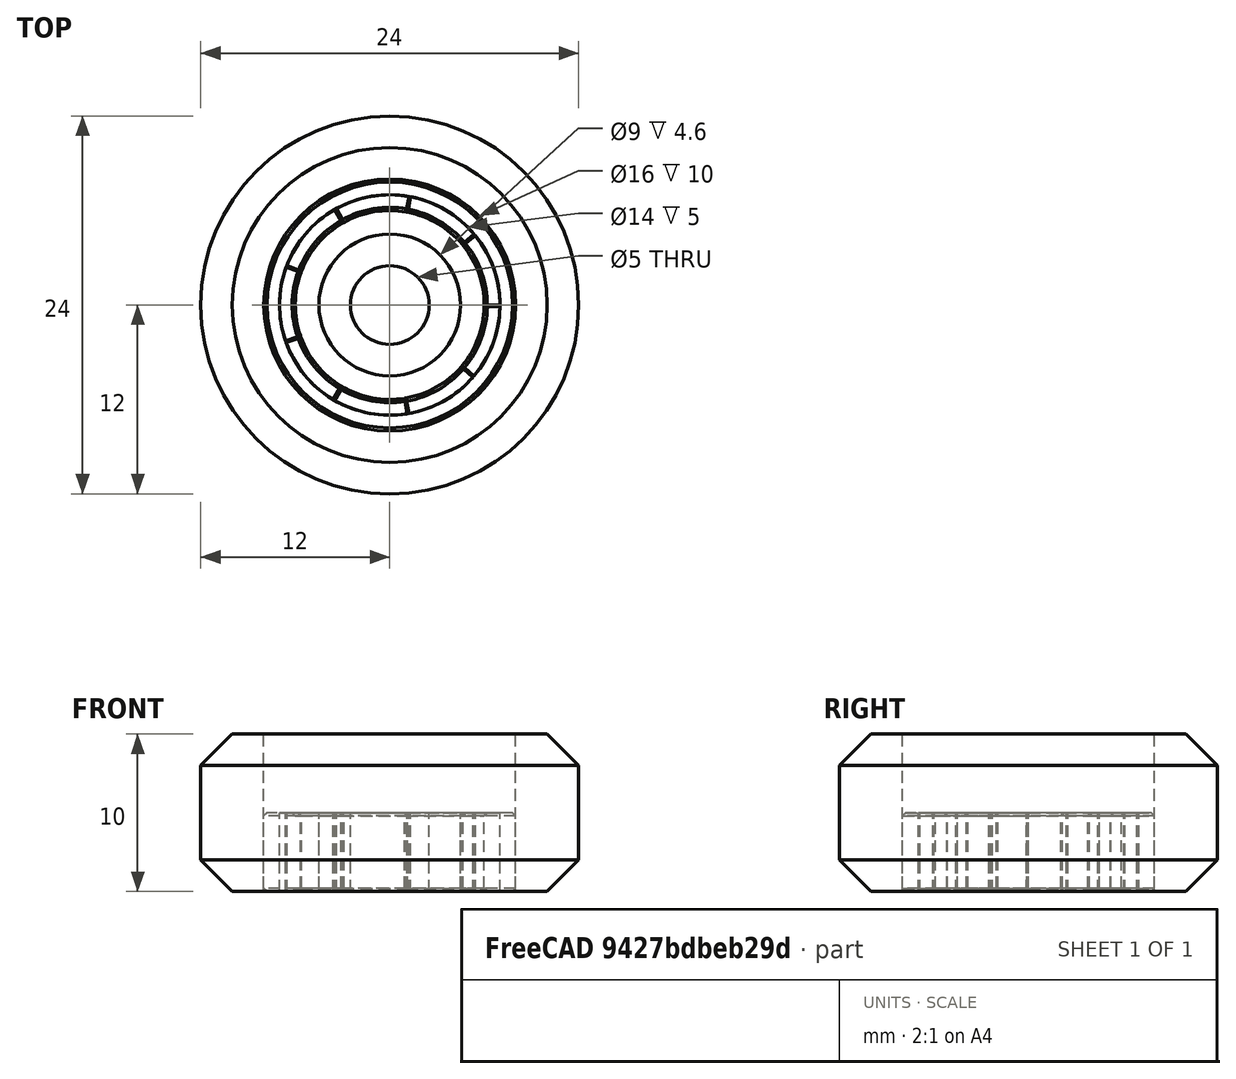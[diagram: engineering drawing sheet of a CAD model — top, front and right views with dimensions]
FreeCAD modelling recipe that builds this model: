
FCSTD DOCUMENT  (FreeCAD 0.19R23578 (Git))
Label: vwheels
License: All rights reserved
LicenseURL: http://en.wikipedia.org/wiki/All_rights_reserved
objects: Part::Cylinder×18, Part::Cut×9, Part::Chamfer×5, App::Part×4, Part::FeaturePython×2, Part::MultiFuse×2
note: 36 computed .brp shape members not serialized (recipe doc carries the construction recipe); baked Part::Feature solids carry a one-line shape summary decoded from their .brp

FEATURE [Part::Cylinder] Cylinder  label="Exterior"
  Angle = 360
  AttacherType = Attacher::AttachEngine3D
  Height = 5
  Radius = 8
FEATURE [Part::Cylinder] Cylinder001  label="Interior"
  Angle = 360
  AttacherType = Attacher::AttachEngine3D
  Height = 5
  Radius = 2.5
FEATURE [Part::Cylinder] Cylinder002  label="Cilindro"
  Angle = 360
  AttacherType = Attacher::AttachEngine3D
  Height = 5
  Radius = 7
FEATURE [Part::Cut] Cut
  Base = -> Cylinder
  Tool = -> Cylinder002
FEATURE [Part::Chamfer] Chamfer004  label="Exterior001"
  Base = -> Cut
  Edges = 2 edges r=0.2: [Edge1,Edge3]
FEATURE [Part::Cylinder] Cylinder003  label="Cilindro001"
  Angle = 360
  AttacherType = Attacher::AttachEngine3D
  Height = 5
  Radius = 4.5
FEATURE [Part::Cut] Cut001  label="Interior001"
  Base = -> Cylinder003
  Tool = -> Cylinder001
FEATURE [Part::Cylinder] Cylinder004  label="Cilindro002"
  Angle = 39
  AttacherType = Attacher::AttachEngine3D
  Height = 5
  Radius = 7
FEATURE [Part::Cylinder] Cylinder005  label="Cilindro003"
  Angle = 39
  AttacherType = Attacher::AttachEngine3D
  Height = 5
  Radius = 6
FEATURE [Part::Cut] Cut002
  Base = -> Cylinder004
  Tool = -> Cylinder005
FEATURE [Part::Chamfer] Chamfer005
  Base = -> Cut002
  Edges = 2 edges r=0.2: [Edge6,Edge11]
FEATURE [Part::FeaturePython] Array  # Draft array (typed FeaturePython)
  Angle = 360
  ArrayType = 1
  Axis = (0,0,1)
  Base = -> Chamfer005
  Center = (0,0,0)
  IntervalX = (1,0,0)
  IntervalY = (0,1,0)
  IntervalZ = (0,0,1)
  NumberPolar = 9
  NumberX = 2
  NumberY = 2
  NumberZ = 1
FEATURE [Part::Cylinder] Cylinder006  label="Cilindro004"
  Angle = 360
  AttacherType = Attacher::AttachEngine3D
  Height = 4.6
  Placement = pos=(0,0,0.2) rot=(0,0,1;0rad)
  Radius = 6
FEATURE [Part::Cylinder] Cylinder007  label="Cilindro005"
  Angle = 360
  AttacherType = Attacher::AttachEngine3D
  Height = 4.6
  Placement = pos=(0,0,0.2) rot=(0,0,1;0rad)
  Radius = 4.5
FEATURE [Part::Cut] Cut003
  Base = -> Cylinder006
  Tool = -> Cylinder007
FEATURE [Part::MultiFuse] Fusion  label="Medio"
  Shapes = -> [Array,Cut003]
FEATURE [Part::Cylinder] Cylinder013  label="Cilindro009"
  Angle = 39
  AttacherType = Attacher::AttachEngine3D
  Height = 5
  Radius = 6
FEATURE [Part::Cylinder] Cylinder011  label="Cilindro007"
  Angle = 360
  AttacherType = Attacher::AttachEngine3D
  Height = 5
  Radius = 4.5
FEATURE [Part::Cylinder] Cylinder012  label="Cilindro008"
  Angle = 39
  AttacherType = Attacher::AttachEngine3D
  Height = 5
  Radius = 7
FEATURE [Part::Cut] Cut006
  Base = -> Cylinder012
  Tool = -> Cylinder013
FEATURE [Part::Chamfer] Chamfer007
  Base = -> Cut006
  Edges = 2 edges r=0.2: [Edge6,Edge11]
FEATURE [Part::FeaturePython] Array001  # Draft array (typed FeaturePython)
  Angle = 360
  ArrayType = 1
  Axis = (0,0,1)
  Base = -> Chamfer007
  Center = (0,0,0)
  IntervalX = (1,0,0)
  IntervalY = (0,1,0)
  IntervalZ = (0,0,1)
  NumberPolar = 9
  NumberX = 2
  NumberY = 2
  NumberZ = 1
FEATURE [Part::Cylinder] Cylinder009  label="Interior002"
  Angle = 360
  AttacherType = Attacher::AttachEngine3D
  Height = 5
  Radius = 2.5
FEATURE [Part::Cut] Cut005  label="Interior003"
  Base = -> Cylinder011
  Tool = -> Cylinder009
FEATURE [App::Part] Part008
  Group = -> [Cylinder001,Cylinder003,Cut001,Cylinder,Cylinder002,Cut,Chamfer004,Cylinder004,Cylinder005,Cut002,Chamfer005,Array,Cylinder006,Cylinder007,Cut003,Fusion]
  Origin = -> Origin016
FEATURE [Part::Cylinder] Cylinder016  label="Cylindre"
  Angle = 360
  AttacherType = Attacher::AttachEngine3D
  Height = 10
  Radius = 12
FEATURE [Part::Cylinder] Cylinder017  label="Cylindre001"
  Angle = 360
  AttacherType = Attacher::AttachEngine3D
  Height = 10
  Radius = 8
FEATURE [Part::Cut] Cut008
  Base = -> Cylinder016
  Tool = -> Cylinder017
FEATURE [Part::Chamfer] Chamfer008
  Base = -> Cut008
  Edges = 2 edges r=2: [Edge1,Edge3]
FEATURE [Part::Cylinder] Cylinder014  label="Cilindro010"
  Angle = 360
  AttacherType = Attacher::AttachEngine3D
  Height = 4.6
  Placement = pos=(0,0,0.2) rot=(0,0,1;0rad)
  Radius = 6
FEATURE [Part::Cylinder] Cylinder015  label="Cilindro011"
  Angle = 360
  AttacherType = Attacher::AttachEngine3D
  Height = 4.6
  Placement = pos=(0,0,0.2) rot=(0,0,1;0rad)
  Radius = 4.5
FEATURE [Part::Cut] Cut007
  Base = -> Cylinder014
  Tool = -> Cylinder015
FEATURE [Part::MultiFuse] Fusion001  label="Medio001"
  Shapes = -> [Array001,Cut007]
FEATURE [App::Part] Part011
  Group = -> [Cylinder016,Cylinder017,Cut008,Chamfer008]
  Origin = -> Origin019
FEATURE [Part::Cylinder] Cylinder008  label="Exterior002"
  Angle = 360
  AttacherType = Attacher::AttachEngine3D
  Height = 5
  Radius = 8
FEATURE [Part::Cylinder] Cylinder010  label="Cilindro006"
  Angle = 360
  AttacherType = Attacher::AttachEngine3D
  Height = 5
  Radius = 7
FEATURE [Part::Cut] Cut004
  Base = -> Cylinder008
  Tool = -> Cylinder010
FEATURE [Part::Chamfer] Chamfer006  label="Exterior003"
  Base = -> Cut004
  Edges = 2 edges r=0.2: [Edge1,Edge3]
FEATURE [App::Part] Part010
  Group = -> [Cylinder009,Cylinder011,Cut005,Cylinder008,Cylinder010,Cut004,Chamfer006,Cylinder012,Cylinder013,Cut006,Chamfer007,Array001,Cylinder014,Cylinder015,Cut007,Fusion001]
  Origin = -> Origin018
  Placement = pos=(0,0,5) rot=(0,0,1;0rad)
FEATURE [App::Part] Part009  label="Vwheels"
  Group = -> [Part008,Part010,Part011]
  Origin = -> Origin017
